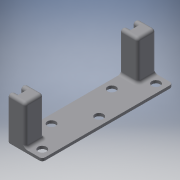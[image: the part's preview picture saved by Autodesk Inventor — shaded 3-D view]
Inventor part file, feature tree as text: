
AUTODESK INVENTOR PART (.ipt)
format: ipt  version: 2018 (Build 220112000, 112)  size: 369,664 bytes
history: native  units: mm
features: reference x20, other x5, fillet x4, sketch x3, extrude x3, plane x1
ambient origin geometry x8: Origin, YZ Plane, XZ Plane, XY Plane, X Axis, Y Axis, Z Axis, Center Point
bodies: Solid1 (feature_tree)
feature tree (36):
  sketch  "Sketch1"  dims[d0=0.25mm d1=0.25mm]
  plane  "Work Plane1"
  extrude  "Extrusion1"  Depth=0.25mm
  extrude  "Extrusion2"  Depth=0.25mm
  extrude  "Extrusion3"  Depth=2.0mm
  fillet  "Fillet1"  Radius=4.0mm
  fillet  "Fillet2"  Radius=18.962mm
  fillet  "Fillet3"  Radius=10.0mm
  fillet  "Fillet4"  Radius=6.0mm
  reference  "Reference1"
  reference  "Reference2"
  reference  "Reference3"
  reference  "Reference4"
  reference  "Reference5"
  reference  "Reference6"
  reference  "Reference7"
  reference  "Reference8"
  reference  "Reference9"
  reference  "Reference10"
  reference  "Reference11"
  reference  "Reference12"
  reference  "Reference13"
  reference  "Reference14"
  reference  "Reference15"
  reference  "Reference16"
  reference  "Reference17"
  reference  "Reference18"
  reference  "Reference19"
  reference  "Reference20"
  sketch  "Sketch2"  dims[d2=0.25mm d3=0.25mm]
  sketch  "Sketch3"  dims[d4=3.0mm d5=2.0mm d6=4.0mm d7=18.962mm d8=10.0mm d9=0.0mm d10=6.0mm d11=1.0mm d12=0.0mm d13=3.0mm d14=3.0mm d15=3.0mm d16=3.0mm d17=3.0mm d18=6.0mm d19=3.0mm d20=3.0mm d21=1.0mm d22=0.0mm d23=1.0mm d24=1.0mm d25=1.0mm d26=1.0mm]
  other  "<userpath>\OneDrive\Documents\Inventor\TSA\2018\Animatronics\Tortoise\Turtle3.iam"
  other  "Turtle3.iam"
  other  "Frame - Copy:1"
  other  "SyringeAttachment:6"
  other  "SyringeAttachment:5"
